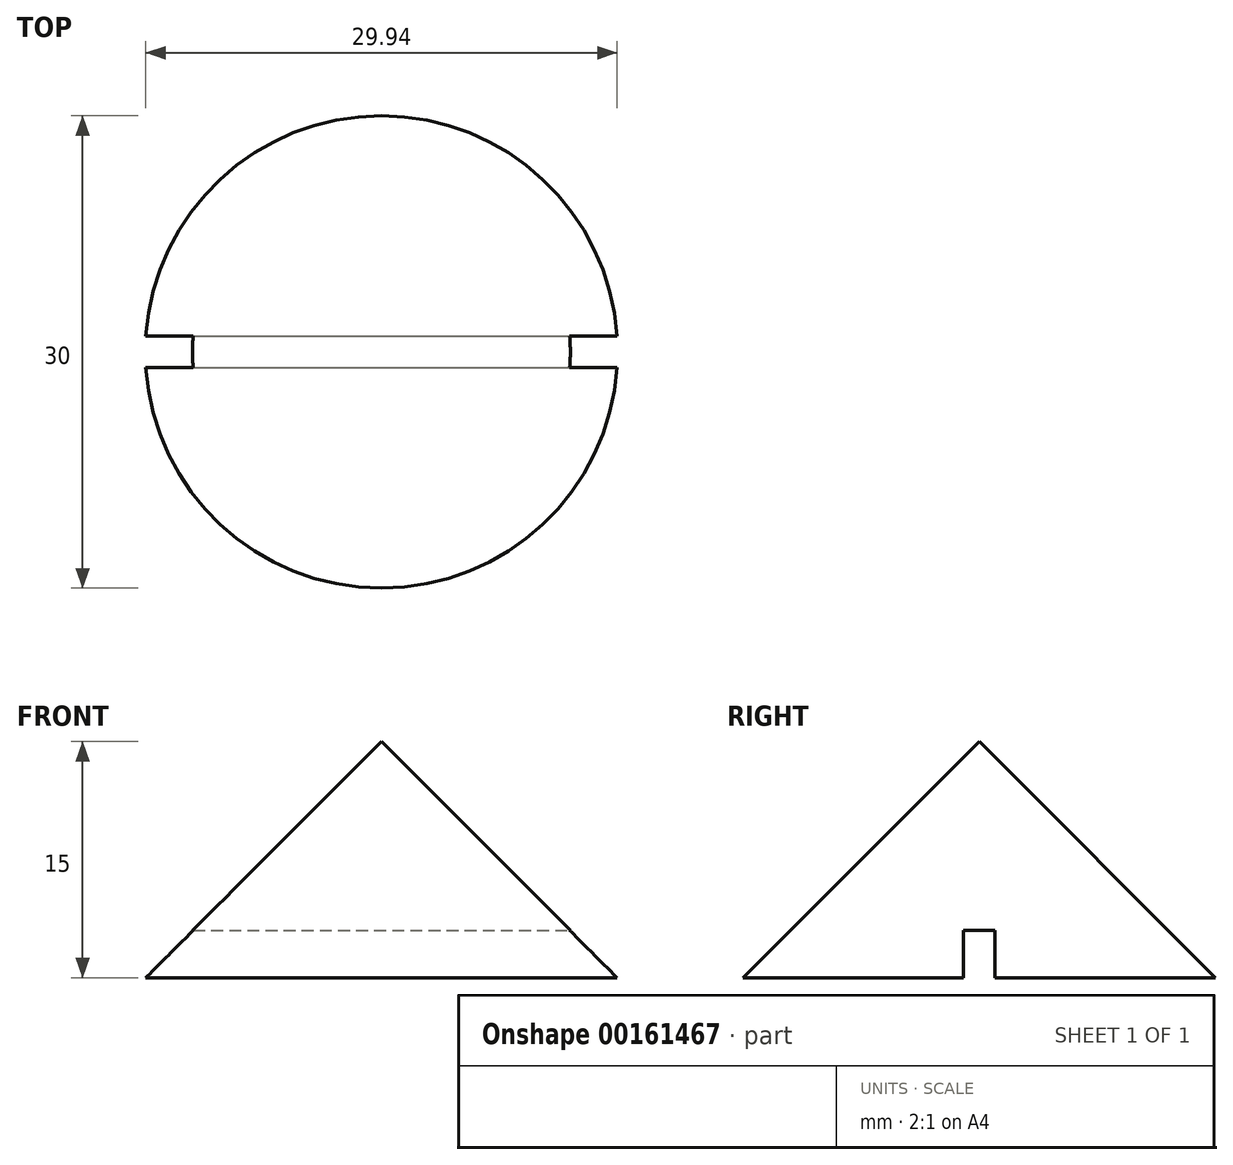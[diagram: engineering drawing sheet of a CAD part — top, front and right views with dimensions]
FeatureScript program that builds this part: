
annotation { "Feature Type Name" : "Feature", "Feature Type Description" : "" }
export const myFeature = defineFeature(function(context is Context, id is Id, definition is map)
    precondition{}
    {
        {
            var Q0;
            Q0=qCreatedBy(makeId("Front.planeOp"),FACE);
            var sketch = newSketch(context, id + "F0", { "sketchPlane" : qUnion([Q0])});
            skLineSegment(sketch, "E0", {"start": v(0, 0) * mm, "end": v(-15, 0) * mm});
            skLineSegment(sketch, "E1", {"start": v(-15, 0) * mm, "end": v(0, 15) * mm});
            skLineSegment(sketch, "E2", {"start": v(0, 15) * mm, "end": v(0, 0) * mm});
            skSolve(sketch);
        }
        {
            var Q0;
            Q0=makeQuery(id+"F0.imprint","IMPRINT",FACE,{"disambiguationData":[TD([[makeQuery(id+"F0.imprint","IMPRINT",EDGE,{"derivedFrom":sQuery(id+"F0.wireOp",EDGE,"E0")}),-1.0]])]});
            var Q1;
            Q1=sQuery(id+"F0.wireOp",EDGE,"E2");
            revolve(context, id + "F1", {"entities" : qUnion([Q0]), "axis" : qUnion([Q1]), "revolveType" : RevolveType.FULL});
        }
        {
            var Q0;
            Q0=makeQuery(id+"F1.opRevolve","SWEPT_FACE",FACE,{"disambiguationData":[OSD([sQuery(id+"F0.wireOp",EDGE,"E0")])]});
            var sketch = newSketch(context, id + "F2", { "sketchPlane" : qUnion([Q0])});
            skLineSegment(sketch, "E3.bottom", {"start": v(-31.41, 1) * mm, "end": v(35.52, 1) * mm});
            skLineSegment(sketch, "E3.top", {"start": v(-31.41, -1) * mm, "end": v(35.52, -1) * mm});
            skLineSegment(sketch, "E3.left", {"start": v(-31.41, 1) * mm, "end": v(-31.41, -1) * mm});
            skLineSegment(sketch, "E3.right", {"start": v(35.52, 1) * mm, "end": v(35.52, -1) * mm});
            skSolve(sketch);
        }
        {
            var Q0;
            {var subQ0=sQuery(id+"F2.wireOp",EDGE,"E3.bottom");var subQ1=makeQuery(id+"F1.opRevolve","SWEPT_EDGE",EDGE,{"disambiguationData":[OSD([sQuery(id+"F0.wireOp",EDGE,"E0"),sQuery(id+"F0.wireOp",EDGE,"E1")])]});var subQ2=makeQuery(id+"F2.imprint","INTERSECT",VERTEX,{"disambiguationData":[OD(0.0)],"derivedFrom":[subQ1,subQ0]});Q0=makeQuery(id+"F2.imprint","IMPRINT",FACE,{"disambiguationData":[TD([[makeQuery(id+"F2.imprint","IMPRINT",EDGE,{"disambiguationData":[TD([[subQ2,-1.0]])],"derivedFrom":subQ0}),-1.0]])]});}
            extrude(context, id + "F3", {"entities" : qUnion([Q0]), "operationType" : NewBodyOperationType.REMOVE, "oppositeDirection" : true, "depth" : 3 * mm});
        }
    });
